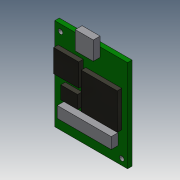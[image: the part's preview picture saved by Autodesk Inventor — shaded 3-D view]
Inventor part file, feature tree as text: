
AUTODESK INVENTOR PART (.ipt)
format: ipt  version: 2018.3 (Build 223284000, 284)  size: 982,016 bytes
history: native  units: in
note: dims shown in document units (in); Inventor stores cm internally (conversion verified against a paired STEP export)
features: extrude x3, other x2, sketch x1, hole x1
ambient origin geometry x8: Origin, YZ Plane, XZ Plane, XY Plane, X Axis, Y Axis, Z Axis, Center Point
bodies: Solid1 (feature_tree)
feature tree (7):
  sketch  "Sketch1"  dims[d0=0.6299in d54=0.7953in d67=0.34in d68=0.265in d69=0.345in d70=0.265in d160=0.0394in d161=0.0in d162=0.0394in d163=0.0in d164=0.0591in d165=0.0in d166=0.0394in d167=0.75in d168=0.375in d169=0.25in d170=0.5635in d171=1.0in d172=0.8108in d173=0.685in d175=0.3937in d232=0.53in]
  extrude  "Extrusion1"  Depth=0.7953in
  extrude  "Extrusion2"  Depth=0.3937in
  extrude  "Extrusion3"  Depth=0.3937in
  hole  "Hole1"  [1 undecoded]
  other  "Image3"
  other  "Image4"
note: 1 required parameter value undecoded (feature->parameter linkage not recoverable at this tier; creation-order binding heuristic only, values carry confidence <= 0.55)
